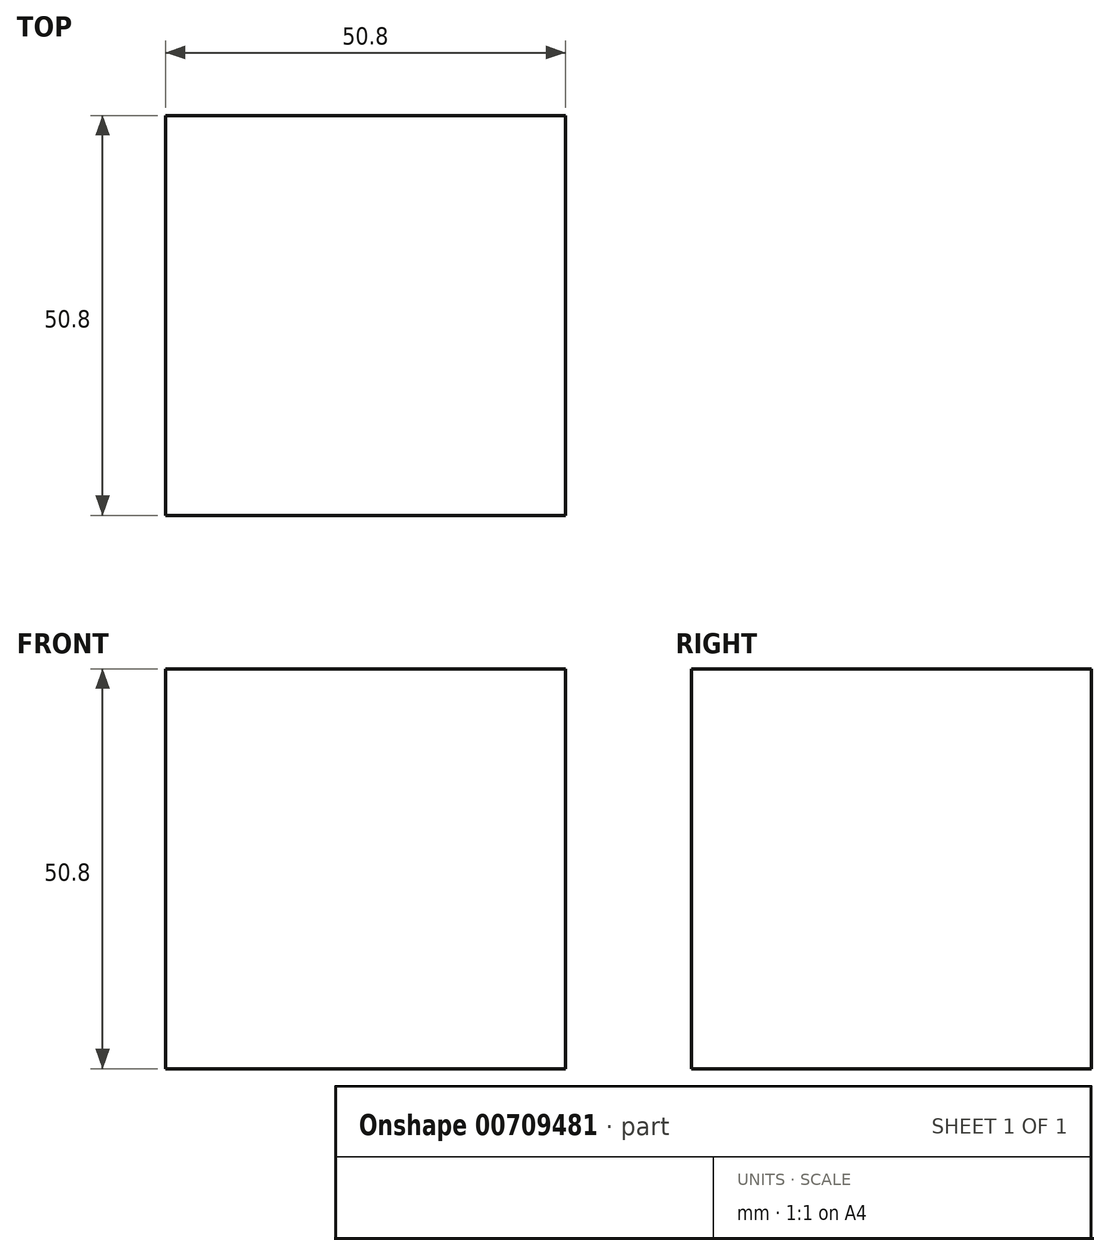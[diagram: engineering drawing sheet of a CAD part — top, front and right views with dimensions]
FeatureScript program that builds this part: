
annotation { "Feature Type Name" : "Feature", "Feature Type Description" : "" }
export const myFeature = defineFeature(function(context is Context, id is Id, definition is map)
    precondition{}
    {
        {
            var Q0;
            Q0=qCreatedBy(makeId("Top.planeOp"),FACE);
            var sketch = newSketch(context, id + "F0", { "sketchPlane" : qUnion([Q0])});
            skLineSegment(sketch, "E0.bottom", {"start": v(25.4, -25.4) * mm, "end": v(-25.4, -25.4) * mm});
            skLineSegment(sketch, "E0.top", {"start": v(25.4, 25.4) * mm, "end": v(-25.4, 25.4) * mm});
            skLineSegment(sketch, "E0.left", {"start": v(25.4, -25.4) * mm, "end": v(25.4, 25.4) * mm});
            skLineSegment(sketch, "E0.right", {"start": v(-25.4, -25.4) * mm, "end": v(-25.4, 25.4) * mm});
            skPoint(sketch, "E0.middle", {"position": v(0, 0) * mm});
            skSolve(sketch);
        }
        {
            var Q0;
            Q0 = qSketchRegion(id + "F0", true);
            extrude(context, id + "F1", {"entities" : qUnion([Q0]), "depth" : 50.8 * mm, "offsetDistance" : 25.4 * mm});
        }
    });
